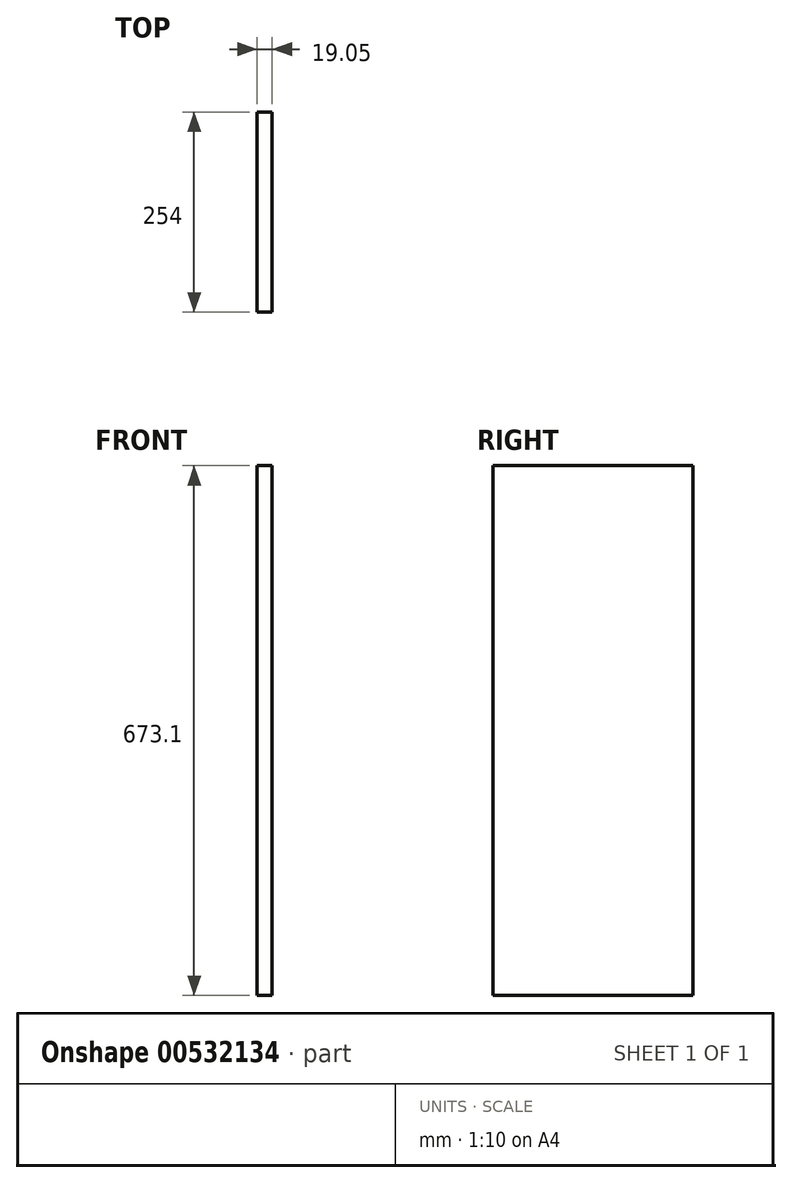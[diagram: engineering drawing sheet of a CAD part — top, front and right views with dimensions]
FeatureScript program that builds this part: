
annotation { "Feature Type Name" : "Feature", "Feature Type Description" : "" }
export const myFeature = defineFeature(function(context is Context, id is Id, definition is map)
    precondition{}
    {
        {
            var Q0;
            Q0=qCreatedBy(makeId("Right.planeOp"),FACE);
            var sketch = newSketch(context, id + "F0", { "sketchPlane" : qUnion([Q0])});
            skLineSegment(sketch, "E0.bottom", {"start": v(127, -336.55) * mm, "end": v(-127, -336.55) * mm});
            skLineSegment(sketch, "E0.top", {"start": v(127, 336.55) * mm, "end": v(-127, 336.55) * mm});
            skLineSegment(sketch, "E0.left", {"start": v(127, -336.55) * mm, "end": v(127, 336.55) * mm});
            skLineSegment(sketch, "E0.right", {"start": v(-127, -336.55) * mm, "end": v(-127, 336.55) * mm});
            skPoint(sketch, "E0.middle", {"position": v(0, 0) * mm});
            skSolve(sketch);
        }
        {
            var Q0;
            Q0 = qSketchRegion(id + "F0", true);
            extrude(context, id + "F1", {"entities" : qUnion([Q0]), "depth" : 19.05 * mm, "offsetDistance" : 25.4 * mm});
        }
    });
